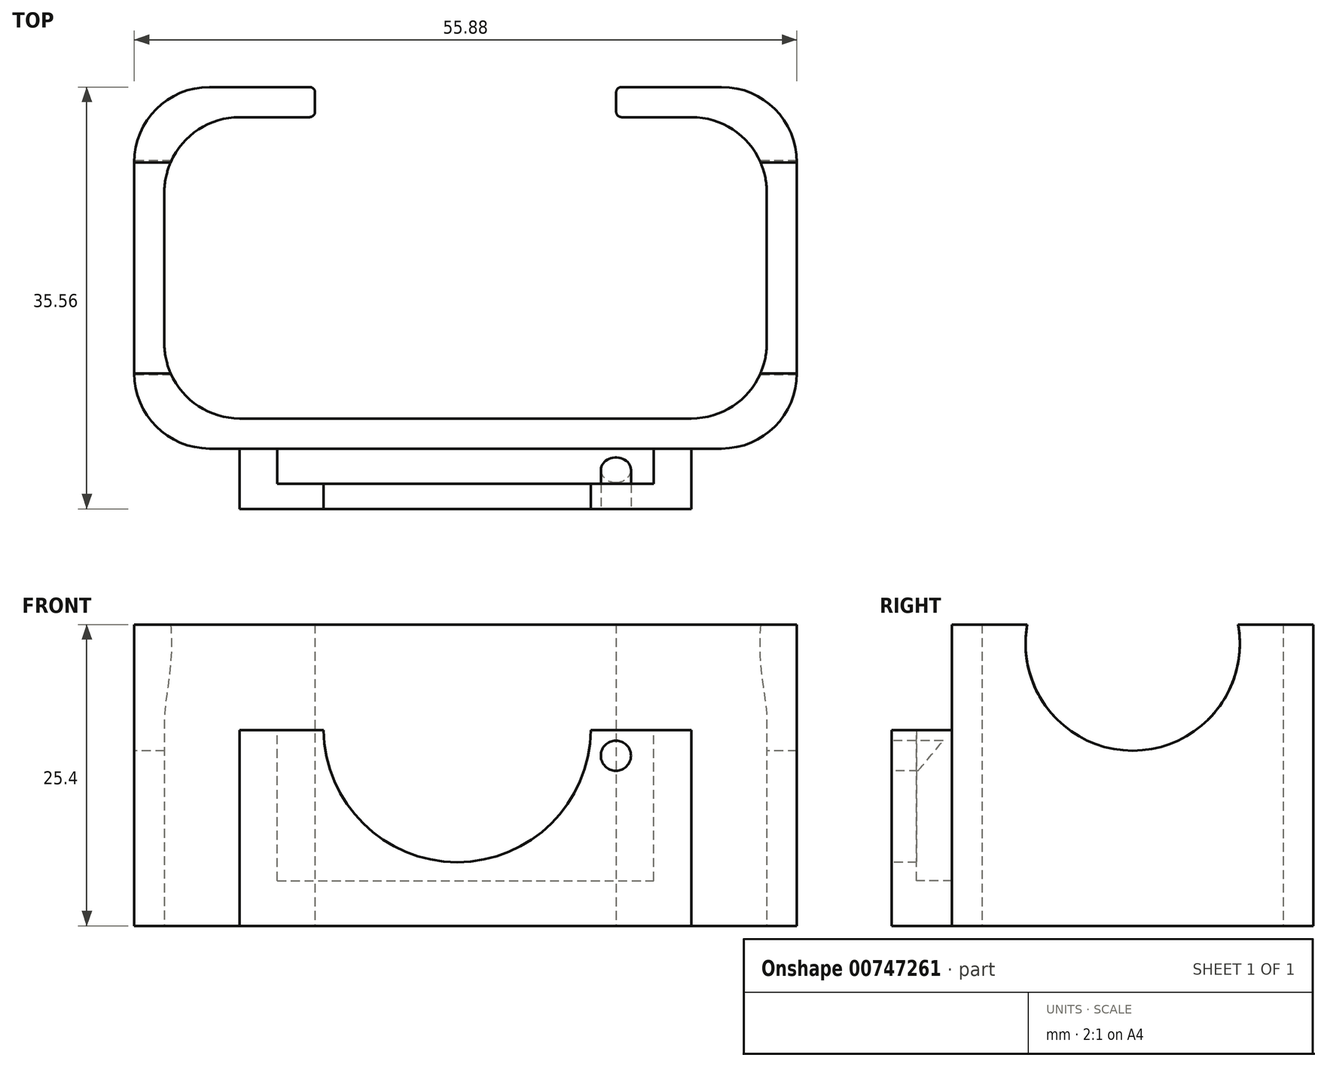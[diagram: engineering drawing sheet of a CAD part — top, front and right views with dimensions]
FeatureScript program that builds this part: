
annotation { "Feature Type Name" : "Feature", "Feature Type Description" : "" }
export const myFeature = defineFeature(function(context is Context, id is Id, definition is map)
    precondition{}
    {
        {
            var Q0;
            Q0=qCreatedBy(makeId("Top.planeOp"),FACE);
            var sketch = newSketch(context, id + "F0", { "sketchPlane" : qUnion([Q0])});
            skLineSegment(sketch, "E0", {"start": v(6.35, 0) * mm, "end": v(49.53, 0) * mm});
            skLineSegment(sketch, "E1", {"start": v(55.88, 6.35) * mm, "end": v(55.88, 24.13) * mm});
            skLineSegment(sketch, "E2", {"start": v(49.53, 30.48) * mm, "end": v(41.1, 30.48) * mm});
            skLineSegment(sketch, "E3", {"start": v(40.64, 30.03) * mm, "end": v(40.64, 28.4) * mm});
            skLineSegment(sketch, "E4", {"start": v(41.1, 27.94) * mm, "end": v(46.99, 27.94) * mm});
            skLineSegment(sketch, "E5", {"start": v(53.34, 21.6) * mm, "end": v(53.34, 8.9) * mm});
            skLineSegment(sketch, "E6", {"start": v(46.99, 2.54) * mm, "end": v(8.89, 2.54) * mm});
            skLineSegment(sketch, "E7", {"start": v(2.54, 8.89) * mm, "end": v(2.54, 21.59) * mm});
            skLineSegment(sketch, "E8", {"start": v(8.89, 27.94) * mm, "end": v(14.79, 27.94) * mm});
            skLineSegment(sketch, "E9", {"start": v(15.24, 28.4) * mm, "end": v(15.24, 30.03) * mm});
            skLineSegment(sketch, "E10", {"start": v(14.79, 30.48) * mm, "end": v(6.35, 30.48) * mm});
            skLineSegment(sketch, "E11", {"start": v(0, 24.13) * mm, "end": v(0, 6.35) * mm});
            skPoint(sketch, "E12.visualSharp", {"position": v(2.54, 27.94) * mm});
            skArc(sketch, "E12.filletArc", {"start": v(8.89, 27.94) * mm, "mid": v(4.4, 26.08) * mm, "end": v(2.54, 21.59) * mm});
            skPoint(sketch, "E13.visualSharp", {"position": v(2.54, 2.54) * mm});
            skArc(sketch, "E13.filletArc", {"start": v(2.54, 8.89) * mm, "mid": v(4.4, 4.4) * mm, "end": v(8.89, 2.54) * mm});
            skPoint(sketch, "E14.visualSharp", {"position": v(53.34, 2.54) * mm});
            skArc(sketch, "E14.filletArc", {"start": v(46.99, 2.54) * mm, "mid": v(51.48, 4.4) * mm, "end": v(53.34, 8.9) * mm});
            skPoint(sketch, "E15.visualSharp", {"position": v(53.34, 27.94) * mm});
            skArc(sketch, "E15.filletArc", {"start": v(53.34, 21.6) * mm, "mid": v(51.48, 26.08) * mm, "end": v(46.99, 27.94) * mm});
            skPoint(sketch, "E16.visualSharp", {"position": v(55.88, 30.48) * mm});
            skArc(sketch, "E16.filletArc", {"start": v(55.88, 24.13) * mm, "mid": v(54.02, 28.62) * mm, "end": v(49.53, 30.48) * mm});
            skPoint(sketch, "E17.visualSharp", {"position": v(55.88, 0) * mm});
            skArc(sketch, "E17.filletArc", {"start": v(49.53, 0) * mm, "mid": v(54.02, 1.86) * mm, "end": v(55.88, 6.35) * mm});
            skPoint(sketch, "E18.visualSharp", {"position": v(0, 0) * mm});
            skArc(sketch, "E18.filletArc", {"start": v(0, 6.35) * mm, "mid": v(1.86, 1.86) * mm, "end": v(6.35, 0) * mm});
            skPoint(sketch, "E19.visualSharp", {"position": v(0, 30.48) * mm});
            skArc(sketch, "E19.filletArc", {"start": v(6.35, 30.48) * mm, "mid": v(1.86, 28.62) * mm, "end": v(0, 24.13) * mm});
            skPoint(sketch, "E20.visualSharp", {"position": v(15.24, 30.48) * mm});
            skArc(sketch, "E20.filletArc", {"start": v(15.24, 30.03) * mm, "mid": v(15.1, 30.35) * mm, "end": v(14.79, 30.48) * mm});
            skPoint(sketch, "E21.visualSharp", {"position": v(15.24, 27.94) * mm});
            skArc(sketch, "E21.filletArc", {"start": v(14.79, 27.94) * mm, "mid": v(15.1, 28.07) * mm, "end": v(15.24, 28.4) * mm});
            skPoint(sketch, "E22.visualSharp", {"position": v(40.64, 30.48) * mm});
            skArc(sketch, "E22.filletArc", {"start": v(41.1, 30.48) * mm, "mid": v(40.77, 30.35) * mm, "end": v(40.64, 30.03) * mm});
            skPoint(sketch, "E23.visualSharp", {"position": v(40.64, 27.94) * mm});
            skArc(sketch, "E23.filletArc", {"start": v(40.64, 28.4) * mm, "mid": v(40.77, 28.07) * mm, "end": v(41.1, 27.94) * mm});
            skSolve(sketch);
        }
        {
            var Q0;
            Q0 = qSketchRegion(id + "F0", true);
            extrude(context, id + "F1", {"entities" : qUnion([Q0]), "depth" : 25.4 * mm, "offsetDistance" : 25.4 * mm});
        }
        {
            var Q0;
            Q0=makeQuery(id+"F1.opExtrude","SWEPT_FACE",FACE,{"disambiguationData":[OSD([sQuery(id+"F0.wireOp",EDGE,"E11")])]});
            var sketch = newSketch(context, id + "F2", { "sketchPlane" : qUnion([Q0])});
            skLineSegment(sketch, "E24", {"start": v(-24.13, 25.4) * mm, "end": v(-6.35, 25.4) * mm});
            skArc(sketch, "E25", {"start": v(-24.13, 25.4) * mm, "mid": v(-15.24, 14.76) * mm, "end": v(-6.35, 25.4) * mm});
            skSolve(sketch);
        }
        {
            var Q0;
            Q0 = qSketchRegion(id + "F2", true);
            extrude(context, id + "F3", {"entities" : qUnion([Q0]), "operationType" : NewBodyOperationType.REMOVE, "oppositeDirection" : true, "depth" : 101.6 * mm, "offsetDistance" : 25.4 * mm});
        }
        {
            var Q0;
            Q0=makeQuery(id+"F1.opExtrude","SWEPT_FACE",FACE,{"disambiguationData":[OSD([sQuery(id+"F0.wireOp",EDGE,"E0")])]});
            var sketch = newSketch(context, id + "F4", { "sketchPlane" : qUnion([Q0])});
            skPoint(sketch, "E26.oppositeSnap0", {"position": v(49.53, 16.51) * mm});
            skLineSegment(sketch, "E26.bottom", {"start": v(8.9, 0) * mm, "end": v(47, 0) * mm});
            skLineSegment(sketch, "E26.top", {"start": v(8.9, 16.51) * mm, "end": v(47, 16.51) * mm});
            skLineSegment(sketch, "E26.left", {"start": v(8.9, 0) * mm, "end": v(8.9, 16.51) * mm});
            skLineSegment(sketch, "E26.right", {"start": v(47, 0) * mm, "end": v(47, 16.51) * mm});
            skSolve(sketch);
        }
        {
            var Q0;
            Q0 = qSketchRegion(id + "F4", true);
            extrude(context, id + "F5", {"entities" : qUnion([Q0]), "depth" : 5.08 * mm, "offsetDistance" : 25.4 * mm});
        }
        {
            var Q0;
            Q0=makeQuery(id+"F5.opExtrude","SWEPT_FACE",FACE,{"disambiguationData":[OSD([sQuery(id+"F4.wireOp",EDGE,"E26.top")])]});
            var sketch = newSketch(context, id + "F6", { "sketchPlane" : qUnion([Q0])});
            skLineSegment(sketch, "E27.bottom", {"start": v(12.07, 0) * mm, "end": v(43.82, 0) * mm});
            skLineSegment(sketch, "E27.top", {"start": v(12.07, -2.98) * mm, "end": v(43.82, -2.98) * mm});
            skLineSegment(sketch, "E27.left", {"start": v(12.07, 0) * mm, "end": v(12.07, -2.98) * mm});
            skLineSegment(sketch, "E27.right", {"start": v(43.82, 0) * mm, "end": v(43.82, -2.98) * mm});
            skSolve(sketch);
        }
        {
            var Q0;
            Q0 = qSketchRegion(id + "F6", true);
            extrude(context, id + "F7", {"entities" : qUnion([Q0]), "operationType" : NewBodyOperationType.REMOVE, "oppositeDirection" : true, "depth" : 12.7 * mm, "offsetDistance" : 25.4 * mm});
        }
        {
            var Q0;
            Q0=makeQuery(id+"F5.opExtrude","CAP_FACE",FACE,{"disambiguationData":[OSD([sQuery(id+"F4.wireOp",EDGE,"E26.bottom"),sQuery(id+"F4.wireOp",EDGE,"E26.top"),sQuery(id+"F4.wireOp",EDGE,"E26.left"),sQuery(id+"F4.wireOp",EDGE,"E26.right")])],"isStart":false});
            var sketch = newSketch(context, id + "F8", { "sketchPlane" : qUnion([Q0])});
            skLineSegment(sketch, "E28", {"start": v(15.97, 16.51) * mm, "end": v(38.52, 16.51) * mm});
            skArc(sketch, "E29", {"start": v(15.97, 16.51) * mm, "mid": v(27.24, 5.37) * mm, "end": v(38.52, 16.51) * mm});
            skSolve(sketch);
        }
        {
            var Q0;
            Q0 = qSketchRegion(id + "F8", true);
            extrude(context, id + "F9", {"entities" : qUnion([Q0]), "operationType" : NewBodyOperationType.REMOVE, "oppositeDirection" : true, "depth" : 2.54 * mm, "offsetDistance" : 25.4 * mm});
        }
        {
            var Q0;
            Q0=makeQuery(id+"F5.opExtrude","CAP_FACE",FACE,{"disambiguationData":[OSD([sQuery(id+"F4.wireOp",EDGE,"E26.bottom"),sQuery(id+"F4.wireOp",EDGE,"E26.top"),sQuery(id+"F4.wireOp",EDGE,"E26.left"),sQuery(id+"F4.wireOp",EDGE,"E26.right")])],"isStart":false});
            var sketch = newSketch(context, id + "F10", { "sketchPlane" : qUnion([Q0])});
            skCircle(sketch, "E30", {"center": v(40.62, 14.34) * mm, "radius": 1.27 * mm});
            skSolve(sketch);
        }
        {
            var Q0;
            Q0 = qSketchRegion(id + "F10", true);
            extrude(context, id + "F11", {"entities" : qUnion([Q0]), "oppositeDirection" : true, "depth" : 5.08 * mm, "offsetDistance" : 25.4 * mm});
        }
        {
            var Q0;
            Q0=makeQuery(id+"F7.boolean.opBoolean","COPY",FACE,{"derivedFrom":makeQuery(id+"F7.opExtrude","SWEPT_FACE",FACE,{"disambiguationData":[OSD([sQuery(id+"F6.wireOp",EDGE,"E27.right")])]})});
            var sketch = newSketch(context, id + "F12", { "sketchPlane" : qUnion([Q0])});
            skLineSegment(sketch, "E31", {"start": v(0, 16.51) * mm, "end": v(2.98, 12.92) * mm});
            skLineSegment(sketch, "E32", {"start": v(2.98, 12.92) * mm, "end": v(0, 12.92) * mm});
            skLineSegment(sketch, "E33", {"start": v(0, 12.92) * mm, "end": v(0, 16.51) * mm});
            skSolve(sketch);
        }
        {
            var Q0;
            Q0 = qSketchRegion(id + "F12", true);
            extrude(context, id + "F13", {"entities" : qUnion([Q0]), "operationType" : NewBodyOperationType.REMOVE, "depth" : 12.7 * mm, "offsetDistance" : 25.4 * mm});
        }
    });
